# Revit family: Haworth_JiveTable_PebbleAsymmetricalLegs
name_source: partatom
category: Furniture Systems
revit_build: Autodesk Revit 2018 (Build: 20170223_1515(x64)
units: mm (PartAtom-declared; Revit-internal decimal feet)

## family parameters
Always vertical = Yes
Cut with Voids When Loaded = No
OmniClass Number = 23.40.70.14.64.21
OmniClass Title = Systems Furniture
Part Type = Normal
Room Calculation Point = No
Round Connector Dimension = Use Diameter
Shared = No
Work Plane-Based = No

## types (47) — shared parameters
48in x 108in = No
48in x 120in = No
54in x 108in = No
54in x 120in = No
54in x 144in = No
6 Column = No
8 Column = No
Actual Table Depth = 48"
Assembly Code = E2020200
Center Leg Location = 0"
Custom Size = No
Manufacturer = Haworth, Inc.
Max. Depth = 54"
Max. Height = 42"
Max. Width = 144"
Middle Columns = No
Min. Depth = 30"
Min. Height = 16"
Min. Width = 48"
Model = Haworth Jive
Revision Number = 1
Size = Verify Final Dim. w/ Haworth
Standard Depths = 24, 30, 36, 42, 48 in.
Standard Heights = 16, 20, 29 in.
Standard Widths = 48, 60, 72, 84, 96 in.
Support Depth 6 8 Column = 4 29/32"
Table Thickness = 1 3/16"
URL = http://www.haworth.com
URL - Product = http://www.haworth.com
Warranty = http://www.haworth.com

## per-type parameters (varying)
- 24d 48w 16h - Post Extruded Base - With Glides: 24in x 48in=Yes; 24in x 60in=No; 24in x 72in=No; 30in x 48in=No; 30in x 60in=No; 30in x 72in=No; 36in x 60in=No; 36in x 72in=No; 36in x 84in=No; 42in x 84in=No; 42in x 96in=No; 48in x 96in=No; Actual Depth=24"; Actual Height=16"; Actual Table Width=57"; Actual Width=48"; Casters=No; Depth=24"; Description=Haworth Jive Table Pebble Asymmetrical Legs - 24d 48w 16h - Post Extruded Base - With Glides; Glides=Yes; Height=16"; Leg Distance=6"; Leg Height=14 13/16"; Post Extruded Leg=Yes; Post Leg=Yes; Post Round Leg=No; Support Distance=11 1/2"; Support Distance 6 8 Column=1 29/32"; T Leg Extruded=No; Table Radius=12"; Width=48"
- 24d 60w 16h - Post Extruded Base - With Glides: 24in x 48in=No; 24in x 60in=Yes; 24in x 72in=No; 30in x 48in=No; 30in x 60in=No; 30in x 72in=No; 36in x 60in=No; 36in x 72in=No; 36in x 84in=No; 42in x 84in=No; 42in x 96in=No; 48in x 96in=No; Actual Depth=24"; Actual Height=16"; Actual Table Width=60"; Actual Width=60"; Casters=No; Depth=24"; Description=Haworth Jive Table Pebble Asymmetrical Legs - 24d 60w 16h - Post Extruded Base - With Glides; Glides=Yes; Height=16"; Leg Distance=6"; Leg Height=14 13/16"; Post Extruded Leg=Yes; Post Leg=Yes; Post Round Leg=No; Support Distance=11 1/2"; Support Distance 6 8 Column=4 29/32"; T Leg Extruded=No; Table Radius=12"; Width=60"
- 24d 72w 16h - Post Extruded Base - With Glides: 24in x 48in=No; 24in x 60in=No; 24in x 72in=Yes; 30in x 48in=No; 30in x 60in=No; 30in x 72in=No; 36in x 60in=No; 36in x 72in=No; 36in x 84in=No; 42in x 84in=No; 42in x 96in=No; 48in x 96in=No; Actual Depth=24"; Actual Height=16"; Actual Table Width=72"; Actual Width=72"; Casters=No; Depth=24"; Description=Haworth Jive Table Pebble Asymmetrical Legs - 24d 72w 16h - Post Extruded Base - With Glides; Glides=Yes; Height=16"; Leg Distance=6"; Leg Height=14 13/16"; Post Extruded Leg=Yes; Post Leg=Yes; Post Round Leg=No; Support Distance=11 1/2"; Support Distance 6 8 Column=16 29/32"; T Leg Extruded=No; Table Radius=12"; Width=72"
- 36d 60w 16h - Post Extruded Base - With Glides: 24in x 48in=No; 24in x 60in=No; 24in x 72in=No; 30in x 48in=No; 30in x 60in=No; 30in x 72in=No; 36in x 60in=Yes; 36in x 72in=No; 36in x 84in=No; 42in x 84in=No; 42in x 96in=No; 48in x 96in=No; Actual Depth=36"; Actual Height=16"; Actual Table Width=60"; Actual Width=60"; Casters=No; Depth=36"; Description=Haworth Jive Table Pebble Asymmetrical Legs - 36d 60w 16h - Post Extruded Base - With Glides; Glides=Yes; Height=16"; Leg Distance=12"; Leg Height=14 13/16"; Post Extruded Leg=Yes; Post Leg=Yes; Post Round Leg=No; Support Distance=11 1/2"; Support Distance 6 8 Column=4 29/32"; T Leg Extruded=No; Table Radius=18"; Width=60"
- 36d 72w 16h - Post Extruded Base - With Glides: 24in x 48in=No; 24in x 60in=No; 24in x 72in=No; 30in x 48in=No; 30in x 60in=No; 30in x 72in=No; 36in x 60in=No; 36in x 72in=Yes; 36in x 84in=No; 42in x 84in=No; 42in x 96in=No; 48in x 96in=No; Actual Depth=36"; Actual Height=16"; Actual Table Width=72"; Actual Width=72"; Casters=No; Depth=36"; Description=Haworth Jive Table Pebble Asymmetrical Legs - 36d 72w 16h - Post Extruded Base - With Glides; Glides=Yes; Height=16"; Leg Distance=12"; Leg Height=14 13/16"; Post Extruded Leg=Yes; Post Leg=Yes; Post Round Leg=No; Support Distance=11 1/2"; Support Distance 6 8 Column=16 29/32"; T Leg Extruded=No; Table Radius=18"; Width=72"
- 36d 84w 16h - Post Extruded Base - With Glides: 24in x 48in=No; 24in x 60in=No; 24in x 72in=No; 30in x 48in=No; 30in x 60in=No; 30in x 72in=No; 36in x 60in=No; 36in x 72in=No; 36in x 84in=Yes; 42in x 84in=No; 42in x 96in=No; 48in x 96in=No; Actual Depth=36"; Actual Height=16"; Actual Table Width=84"; Actual Width=84"; Casters=No; Depth=36"; Description=Haworth Jive Table Pebble Asymmetrical Legs - 36d 84w 16h - Post Extruded Base - With Glides; Glides=Yes; Height=16"; Leg Distance=12"; Leg Height=14 13/16"; Post Extruded Leg=Yes; Post Leg=Yes; Post Round Leg=No; Support Distance=11 1/2"; Support Distance 6 8 Column=28 29/32"; T Leg Extruded=No; Table Radius=18"; Width=84"
- 30d 48w 20h - Post Extruded Base - With Glides: 24in x 48in=No; 24in x 60in=No; 24in x 72in=No; 30in x 48in=Yes; 30in x 60in=No; 30in x 72in=No; 36in x 60in=No; 36in x 72in=No; 36in x 84in=No; 42in x 84in=No; 42in x 96in=No; 48in x 96in=No; Actual Depth=30"; Actual Height=20"; Actual Table Width=57"; Actual Width=48"; Casters=No; Depth=30"; Description=Haworth Jive Table Pebble Asymmetrical Legs - 30d 48w 20h - Post Extruded Base - With Glides; Glides=Yes; Height=20"; Leg Distance=9"; Leg Height=18 13/16"; Post Extruded Leg=Yes; Post Leg=Yes; Post Round Leg=No; Support Distance=11 1/2"; Support Distance 6 8 Column=1 29/32"; T Leg Extruded=No; Table Radius=15"; Width=48"
- 30d 60w 20h - Post Extruded Base - With Glides: 24in x 48in=No; 24in x 60in=No; 24in x 72in=No; 30in x 48in=No; 30in x 60in=Yes; 30in x 72in=No; 36in x 60in=No; 36in x 72in=No; 36in x 84in=No; 42in x 84in=No; 42in x 96in=No; 48in x 96in=No; Actual Depth=30"; Actual Height=20"; Actual Table Width=60"; Actual Width=60"; Casters=No; Depth=30"; Description=Haworth Jive Table Pebble Asymmetrical Legs - 30d 60w 20h - Post Extruded Base - With Glides; Glides=Yes; Height=20"; Leg Distance=9"; Leg Height=18 13/16"; Post Extruded Leg=Yes; Post Leg=Yes; Post Round Leg=No; Support Distance=11 1/2"; Support Distance 6 8 Column=4 29/32"; T Leg Extruded=No; Table Radius=15"; Width=60"
- 30d 72w 20h - Post Extruded Base - With Glides: 24in x 48in=No; 24in x 60in=No; 24in x 72in=No; 30in x 48in=No; 30in x 60in=No; 30in x 72in=Yes; 36in x 60in=No; 36in x 72in=No; 36in x 84in=No; 42in x 84in=No; 42in x 96in=No; 48in x 96in=No; Actual Depth=30"; Actual Height=20"; Actual Table Width=72"; Actual Width=72"; Casters=No; Depth=30"; Description=Haworth Jive Table Pebble Asymmetrical Legs - 30d 72w 20h - Post Extruded Base - With Glides; Glides=Yes; Height=20"; Leg Distance=9"; Leg Height=18 13/16"; Post Extruded Leg=Yes; Post Leg=Yes; Post Round Leg=No; Support Distance=11 1/2"; Support Distance 6 8 Column=16 29/32"; T Leg Extruded=No; Table Radius=15"; Width=72"
- 36d 60w 20h - Post Extruded Base - With Glides: 24in x 48in=No; 24in x 60in=No; 24in x 72in=No; 30in x 48in=No; 30in x 60in=No; 30in x 72in=No; 36in x 60in=Yes; 36in x 72in=No; 36in x 84in=No; 42in x 84in=No; 42in x 96in=No; 48in x 96in=No; Actual Depth=36"; Actual Height=20"; Actual Table Width=60"; Actual Width=60"; Casters=No; Depth=36"; Description=Haworth Jive Table Pebble Asymmetrical Legs - 36d 60w 20h - Post Extruded Base - With Glides; Glides=Yes; Height=20"; Leg Distance=12"; Leg Height=18 13/16"; Post Extruded Leg=Yes; Post Leg=Yes; Post Round Leg=No; Support Distance=11 1/2"; Support Distance 6 8 Column=4 29/32"; T Leg Extruded=No; Table Radius=18"; Width=60"
- 36d 72w 20h - Post Extruded Base - With Glides: 24in x 48in=No; 24in x 60in=No; 24in x 72in=No; 30in x 48in=No; 30in x 60in=No; 30in x 72in=No; 36in x 60in=No; 36in x 72in=Yes; 36in x 84in=No; 42in x 84in=No; 42in x 96in=No; 48in x 96in=No; Actual Depth=36"; Actual Height=20"; Actual Table Width=72"; Actual Width=72"; Casters=No; Depth=36"; Description=Haworth Jive Table Pebble Asymmetrical Legs - 36d 72w 20h - Post Extruded Base - With Glides; Glides=Yes; Height=20"; Leg Distance=12"; Leg Height=18 13/16"; Post Extruded Leg=Yes; Post Leg=Yes; Post Round Leg=No; Support Distance=11 1/2"; Support Distance 6 8 Column=16 29/32"; T Leg Extruded=No; Table Radius=18"; Width=72"
- 36d 84w 20h - Post Extruded Base - With Glides: 24in x 48in=No; 24in x 60in=No; 24in x 72in=No; 30in x 48in=No; 30in x 60in=No; 30in x 72in=No; 36in x 60in=No; 36in x 72in=No; 36in x 84in=Yes; 42in x 84in=No; 42in x 96in=No; 48in x 96in=No; Actual Depth=36"; Actual Height=20"; Actual Table Width=84"; Actual Width=84"; Casters=No; Depth=36"; Description=Haworth Jive Table Pebble Asymmetrical Legs - 36d 84w 20h - Post Extruded Base - With Glides; Glides=Yes; Height=20"; Leg Distance=12"; Leg Height=18 13/16"; Post Extruded Leg=Yes; Post Leg=Yes; Post Round Leg=No; Support Distance=11 1/2"; Support Distance 6 8 Column=28 29/32"; T Leg Extruded=No; Table Radius=18"; Width=84"
- 30d 48w 29h - Post Extruded Base - With Casters: 24in x 48in=No; 24in x 60in=No; 24in x 72in=No; 30in x 48in=Yes; 30in x 60in=No; 30in x 72in=No; 36in x 60in=No; 36in x 72in=No; 36in x 84in=No; 42in x 84in=No; 42in x 96in=No; 48in x 96in=No; Actual Depth=30"; Actual Height=29"; Actual Table Width=57"; Actual Width=48"; Casters=Yes; Depth=30"; Description=Haworth Jive Table Pebble Asymmetrical Legs - 30d 48w 29h - Post Extruded Base - With Casters; Glides=No; Height=29"; Leg Distance=9"; Leg Height=27 13/16"; Post Extruded Leg=Yes; Post Leg=Yes; Post Round Leg=No; Support Distance=11 1/2"; Support Distance 6 8 Column=1 29/32"; T Leg Extruded=No; Table Radius=15"; Width=48"
- 30d 60w 29h - Post Extruded Base - With Casters: 24in x 48in=No; 24in x 60in=No; 24in x 72in=No; 30in x 48in=No; 30in x 60in=Yes; 30in x 72in=No; 36in x 60in=No; 36in x 72in=No; 36in x 84in=No; 42in x 84in=No; 42in x 96in=No; 48in x 96in=No; Actual Depth=30"; Actual Height=29"; Actual Table Width=60"; Actual Width=60"; Casters=Yes; Depth=30"; Description=Haworth Jive Table Pebble Asymmetrical Legs - 30d 60w 29h - Post Extruded Base - With Casters; Glides=No; Height=29"; Leg Distance=9"; Leg Height=27 13/16"; Post Extruded Leg=Yes; Post Leg=Yes; Post Round Leg=No; Support Distance=11 1/2"; Support Distance 6 8 Column=4 29/32"; T Leg Extruded=No; Table Radius=15"; Width=60"
- 30d 72w 29h - Post Extruded Base - With Casters: 24in x 48in=No; 24in x 60in=No; 24in x 72in=No; 30in x 48in=No; 30in x 60in=No; 30in x 72in=Yes; 36in x 60in=No; 36in x 72in=No; 36in x 84in=No; 42in x 84in=No; 42in x 96in=No; 48in x 96in=No; Actual Depth=30"; Actual Height=29"; Actual Table Width=72"; Actual Width=72"; Casters=Yes; Depth=30"; Description=Haworth Jive Table Pebble Asymmetrical Legs - 30d 72w 29h - Post Extruded Base - With Casters; Glides=No; Height=29"; Leg Distance=9"; Leg Height=27 13/16"; Post Extruded Leg=Yes; Post Leg=Yes; Post Round Leg=No; Support Distance=11 1/2"; Support Distance 6 8 Column=16 29/32"; T Leg Extruded=No; Table Radius=15"; Width=72"
- 36d 60w 29h - Post Extruded Base - With Casters: 24in x 48in=No; 24in x 60in=No; 24in x 72in=No; 30in x 48in=No; 30in x 60in=No; 30in x 72in=No; 36in x 60in=Yes; 36in x 72in=No; 36in x 84in=No; 42in x 84in=No; 42in x 96in=No; 48in x 96in=No; Actual Depth=36"; Actual Height=29"; Actual Table Width=60"; Actual Width=60"; Casters=Yes; Depth=36"; Description=Haworth Jive Table Pebble Asymmetrical Legs - 36d 60w 29h - Post Extruded Base - With Casters; Glides=No; Height=29"; Leg Distance=12"; Leg Height=27 13/16"; Post Extruded Leg=Yes; Post Leg=Yes; Post Round Leg=No; Support Distance=11 1/2"; Support Distance 6 8 Column=4 29/32"; T Leg Extruded=No; Table Radius=18"; Width=60"
- 36d 72w 29h - Post Extruded Base - With Casters: 24in x 48in=No; 24in x 60in=No; 24in x 72in=No; 30in x 48in=No; 30in x 60in=No; 30in x 72in=No; 36in x 60in=No; 36in x 72in=Yes; 36in x 84in=No; 42in x 84in=No; 42in x 96in=No; 48in x 96in=No; Actual Depth=36"; Actual Height=29"; Actual Table Width=72"; Actual Width=72"; Casters=Yes; Depth=36"; Description=Haworth Jive Table Pebble Asymmetrical Legs - 36d 72w 29h - Post Extruded Base - With Casters; Glides=No; Height=29"; Leg Distance=12"; Leg Height=27 13/16"; Post Extruded Leg=Yes; Post Leg=Yes; Post Round Leg=No; Support Distance=11 1/2"; Support Distance 6 8 Column=16 29/32"; T Leg Extruded=No; Table Radius=18"; Width=72"
- 36d 84w 29h - Post Extruded Base - With Casters: 24in x 48in=No; 24in x 60in=No; 24in x 72in=No; 30in x 48in=No; 30in x 60in=No; 30in x 72in=No; 36in x 60in=No; 36in x 72in=No; 36in x 84in=Yes; 42in x 84in=No; 42in x 96in=No; 48in x 96in=No; Actual Depth=36"; Actual Height=29"; Actual Table Width=84"; Actual Width=84"; Casters=Yes; Depth=36"; Description=Haworth Jive Table Pebble Asymmetrical Legs - 36d 84w 29h - Post Extruded Base - With Casters; Glides=No; Height=29"; Leg Distance=12"; Leg Height=27 13/16"; Post Extruded Leg=Yes; Post Leg=Yes; Post Round Leg=No; Support Distance=11 1/2"; Support Distance 6 8 Column=28 29/32"; T Leg Extruded=No; Table Radius=18"; Width=84"
- 30d 48w 29h - Post Extruded Base - With Glides: 24in x 48in=No; 24in x 60in=No; 24in x 72in=No; 30in x 48in=Yes; 30in x 60in=No; 30in x 72in=No; 36in x 60in=No; 36in x 72in=No; 36in x 84in=No; 42in x 84in=No; 42in x 96in=No; 48in x 96in=No; Actual Depth=30"; Actual Height=29"; Actual Table Width=57"; Actual Width=48"; Casters=No; Depth=30"; Description=Haworth Jive Table Pebble Asymmetrical Legs - 30d 48w 29h - Post Extruded Base - With Glides; Glides=Yes; Height=29"; Leg Distance=9"; Leg Height=27 13/16"; Post Extruded Leg=Yes; Post Leg=Yes; Post Round Leg=No; Support Distance=11 1/2"; Support Distance 6 8 Column=1 29/32"; T Leg Extruded=No; Table Radius=15"; Width=48"
- 30d 60w 29h - Post Extruded Base - With Glides: 24in x 48in=No; 24in x 60in=No; 24in x 72in=No; 30in x 48in=No; 30in x 60in=Yes; 30in x 72in=No; 36in x 60in=No; 36in x 72in=No; 36in x 84in=No; 42in x 84in=No; 42in x 96in=No; 48in x 96in=No; Actual Depth=30"; Actual Height=29"; Actual Table Width=60"; Actual Width=60"; Casters=No; Depth=30"; Description=Haworth Jive Table Pebble Asymmetrical Legs - 30d 60w 29h - Post Extruded Base - With Glides; Glides=Yes; Height=29"; Leg Distance=9"; Leg Height=27 13/16"; Post Extruded Leg=Yes; Post Leg=Yes; Post Round Leg=No; Support Distance=11 1/2"; Support Distance 6 8 Column=4 29/32"; T Leg Extruded=No; Table Radius=15"; Width=60"
- 30d 72w 29h - Post Extruded Base - With Glides: 24in x 48in=No; 24in x 60in=No; 24in x 72in=No; 30in x 48in=No; 30in x 60in=No; 30in x 72in=Yes; 36in x 60in=No; 36in x 72in=No; 36in x 84in=No; 42in x 84in=No; 42in x 96in=No; 48in x 96in=No; Actual Depth=30"; Actual Height=29"; Actual Table Width=72"; Actual Width=72"; Casters=No; Depth=30"; Description=Haworth Jive Table Pebble Asymmetrical Legs - 30d 72w 29h - Post Extruded Base - With Glides; Glides=Yes; Height=29"; Leg Distance=9"; Leg Height=27 13/16"; Post Extruded Leg=Yes; Post Leg=Yes; Post Round Leg=No; Support Distance=11 1/2"; Support Distance 6 8 Column=16 29/32"; T Leg Extruded=No; Table Radius=15"; Width=72"
- 36d 60w 29h - Post Extruded Base - With Glides: 24in x 48in=No; 24in x 60in=No; 24in x 72in=No; 30in x 48in=No; 30in x 60in=No; 30in x 72in=No; 36in x 60in=Yes; 36in x 72in=No; 36in x 84in=No; 42in x 84in=No; 42in x 96in=No; 48in x 96in=No; Actual Depth=36"; Actual Height=29"; Actual Table Width=60"; Actual Width=60"; Casters=No; Depth=36"; Description=Haworth Jive Table Pebble Asymmetrical Legs - 36d 60w 29h - Post Extruded Base - With Glides; Glides=Yes; Height=29"; Leg Distance=12"; Leg Height=27 13/16"; Post Extruded Leg=Yes; Post Leg=Yes; Post Round Leg=No; Support Distance=11 1/2"; Support Distance 6 8 Column=4 29/32"; T Leg Extruded=No; Table Radius=18"; Width=60"
- 36d 72w 29h - Post Extruded Base - With Glides: 24in x 48in=No; 24in x 60in=No; 24in x 72in=No; 30in x 48in=No; 30in x 60in=No; 30in x 72in=No; 36in x 60in=No; 36in x 72in=Yes; 36in x 84in=No; 42in x 84in=No; 42in x 96in=No; 48in x 96in=No; Actual Depth=36"; Actual Height=29"; Actual Table Width=72"; Actual Width=72"; Casters=No; Depth=36"; Description=Haworth Jive Table Pebble Asymmetrical Legs - 36d 72w 29h - Post Extruded Base - With Glides; Glides=Yes; Height=29"; Leg Distance=12"; Leg Height=27 13/16"; Post Extruded Leg=Yes; Post Leg=Yes; Post Round Leg=No; Support Distance=11 1/2"; Support Distance 6 8 Column=16 29/32"; T Leg Extruded=No; Table Radius=18"; Width=72"
- 36d 84w 29h - Post Extruded Base - With Glides: 24in x 48in=No; 24in x 60in=No; 24in x 72in=No; 30in x 48in=No; 30in x 60in=No; 30in x 72in=No; 36in x 60in=No; 36in x 72in=No; 36in x 84in=Yes; 42in x 84in=No; 42in x 96in=No; 48in x 96in=No; Actual Depth=36"; Actual Height=29"; Actual Table Width=84"; Actual Width=84"; Casters=No; Depth=36"; Description=Haworth Jive Table Pebble Asymmetrical Legs - 36d 84w 29h - Post Extruded Base - With Glides; Glides=Yes; Height=29"; Leg Distance=12"; Leg Height=27 13/16"; Post Extruded Leg=Yes; Post Leg=Yes; Post Round Leg=No; Support Distance=11 1/2"; Support Distance 6 8 Column=28 29/32"; T Leg Extruded=No; Table Radius=18"; Width=84"
- 42d 84w 29h - Post Extruded Base - With Glides: 24in x 48in=No; 24in x 60in=No; 24in x 72in=No; 30in x 48in=No; 30in x 60in=No; 30in x 72in=No; 36in x 60in=No; 36in x 72in=No; 36in x 84in=No; 42in x 84in=Yes; 42in x 96in=No; 48in x 96in=No; Actual Depth=42"; Actual Height=29"; Actual Table Width=84"; Actual Width=84"; Casters=No; Depth=42"; Description=Haworth Jive Table Pebble Asymmetrical Legs - 42d 84w 29h - Post Extruded Base - With Glides; Glides=Yes; Height=29"; Leg Distance=15"; Leg Height=27 13/16"; Post Extruded Leg=Yes; Post Leg=Yes; Post Round Leg=No; Support Distance=11 1/2"; Support Distance 6 8 Column=28 29/32"; T Leg Extruded=No; Table Radius=21"; Width=84"
- 42d 96w 29h - Post Extruded Base - With Glides: 24in x 48in=No; 24in x 60in=No; 24in x 72in=No; 30in x 48in=No; 30in x 60in=No; 30in x 72in=No; 36in x 60in=No; 36in x 72in=No; 36in x 84in=No; 42in x 84in=No; 42in x 96in=Yes; 48in x 96in=No; Actual Depth=42"; Actual Height=29"; Actual Table Width=96"; Actual Width=96"; Casters=No; Depth=42"; Description=Haworth Jive Table Pebble Asymmetrical Legs - 42d 96w 29h - Post Extruded Base - With Glides; Glides=Yes; Height=29"; Leg Distance=15"; Leg Height=27 13/16"; Post Extruded Leg=Yes; Post Leg=Yes; Post Round Leg=No; Support Distance=11 1/2"; Support Distance 6 8 Column=40 29/32"; T Leg Extruded=No; Table Radius=21"; Width=96"
- 48d 96w 29h - Post Extruded Base - With Glides: 24in x 48in=No; 24in x 60in=No; 24in x 72in=No; 30in x 48in=No; 30in x 60in=No; 30in x 72in=No; 36in x 60in=No; 36in x 72in=No; 36in x 84in=No; 42in x 84in=No; 42in x 96in=No; 48in x 96in=Yes; Actual Depth=42"; Actual Height=29"; Actual Table Width=96"; Actual Width=96"; Casters=No; Depth=48"; Description=Haworth Jive Table Pebble Asymmetrical Legs - 48d 96w 29h - Post Extruded Base - With Glides; Glides=Yes; Height=29"; Leg Distance=15"; Leg Height=27 13/16"; Post Extruded Leg=Yes; Post Leg=Yes; Post Round Leg=No; Support Distance=11 1/2"; Support Distance 6 8 Column=40 29/32"; T Leg Extruded=No; Table Radius=21"; Width=96"
- 30d 48w 29h - Post Round Base - With Casters: 24in x 48in=No; 24in x 60in=No; 24in x 72in=No; 30in x 48in=Yes; 30in x 60in=No; 30in x 72in=No; 36in x 60in=No; 36in x 72in=No; 36in x 84in=No; 42in x 84in=No; 42in x 96in=No; 48in x 96in=No; Actual Depth=30"; Actual Height=29"; Actual Table Width=57"; Actual Width=48"; Casters=Yes; Depth=30"; Description=Haworth Jive Table Pebble Asymmetrical Legs - 30d 48w 29h - Post Round Base - With Casters; Glides=No; Height=29"; Leg Distance=9"; Leg Height=27 13/16"; Post Extruded Leg=No; Post Leg=Yes; Post Round Leg=Yes; Support Distance=11 1/2"; Support Distance 6 8 Column=1 29/32"; T Leg Extruded=No; Table Radius=15"; Width=48"
- 30d 60w 29h - Post Round Base - With Casters: 24in x 48in=No; 24in x 60in=No; 24in x 72in=No; 30in x 48in=No; 30in x 60in=Yes; 30in x 72in=No; 36in x 60in=No; 36in x 72in=No; 36in x 84in=No; 42in x 84in=No; 42in x 96in=No; 48in x 96in=No; Actual Depth=30"; Actual Height=29"; Actual Table Width=60"; Actual Width=60"; Casters=Yes; Depth=30"; Description=Haworth Jive Table Pebble Asymmetrical Legs - 30d 60w 29h - Post Round Base - With Casters; Glides=No; Height=29"; Leg Distance=9"; Leg Height=27 13/16"; Post Extruded Leg=No; Post Leg=Yes; Post Round Leg=Yes; Support Distance=11 1/2"; Support Distance 6 8 Column=4 29/32"; T Leg Extruded=No; Table Radius=15"; Width=60"
- 30d 72w 29h - Post Round Base - With Casters: 24in x 48in=No; 24in x 60in=No; 24in x 72in=No; 30in x 48in=No; 30in x 60in=No; 30in x 72in=Yes; 36in x 60in=No; 36in x 72in=No; 36in x 84in=No; 42in x 84in=No; 42in x 96in=No; 48in x 96in=No; Actual Depth=30"; Actual Height=29"; Actual Table Width=72"; Actual Width=72"; Casters=Yes; Depth=30"; Description=Haworth Jive Table Pebble Asymmetrical Legs - 30d 72w 29h - Post Round Base - With Casters; Glides=No; Height=29"; Leg Distance=9"; Leg Height=27 13/16"; Post Extruded Leg=No; Post Leg=Yes; Post Round Leg=Yes; Support Distance=11 1/2"; Support Distance 6 8 Column=16 29/32"; T Leg Extruded=No; Table Radius=15"; Width=72"
- 36d 60w 29h - Post Round Base - With Casters: 24in x 48in=No; 24in x 60in=No; 24in x 72in=No; 30in x 48in=No; 30in x 60in=No; 30in x 72in=No; 36in x 60in=Yes; 36in x 72in=No; 36in x 84in=No; 42in x 84in=No; 42in x 96in=No; 48in x 96in=No; Actual Depth=36"; Actual Height=29"; Actual Table Width=60"; Actual Width=60"; Casters=Yes; Depth=36"; Description=Haworth Jive Table Pebble Asymmetrical Legs - 36d 60w 29h - Post Round Base - With Casters; Glides=No; Height=29"; Leg Distance=12"; Leg Height=27 13/16"; Post Extruded Leg=No; Post Leg=Yes; Post Round Leg=Yes; Support Distance=11 1/2"; Support Distance 6 8 Column=4 29/32"; T Leg Extruded=No; Table Radius=18"; Width=60"
- 36d 72w 29h - Post Round Base - With Casters: 24in x 48in=No; 24in x 60in=No; 24in x 72in=No; 30in x 48in=No; 30in x 60in=No; 30in x 72in=No; 36in x 60in=No; 36in x 72in=Yes; 36in x 84in=No; 42in x 84in=No; 42in x 96in=No; 48in x 96in=No; Actual Depth=36"; Actual Height=29"; Actual Table Width=72"; Actual Width=72"; Casters=Yes; Depth=36"; Description=Haworth Jive Table Pebble Asymmetrical Legs - 36d 72w 29h - Post Round Base - With Casters; Glides=No; Height=29"; Leg Distance=12"; Leg Height=27 13/16"; Post Extruded Leg=No; Post Leg=Yes; Post Round Leg=Yes; Support Distance=11 1/2"; Support Distance 6 8 Column=16 29/32"; T Leg Extruded=No; Table Radius=18"; Width=72"
- 30d 48w 29h - Post Round Base - With Glides: 24in x 48in=No; 24in x 60in=No; 24in x 72in=No; 30in x 48in=Yes; 30in x 60in=No; 30in x 72in=No; 36in x 60in=No; 36in x 72in=No; 36in x 84in=No; 42in x 84in=No; 42in x 96in=No; 48in x 96in=No; Actual Depth=30"; Actual Height=29"; Actual Table Width=57"; Actual Width=48"; Casters=No; Depth=30"; Description=Haworth Jive Table Pebble Asymmetrical Legs - 30d 48w 29h - Post Round Base - With Glides; Glides=Yes; Height=29"; Leg Distance=9"; Leg Height=27 13/16"; Post Extruded Leg=No; Post Leg=Yes; Post Round Leg=Yes; Support Distance=11 1/2"; Support Distance 6 8 Column=1 29/32"; T Leg Extruded=No; Table Radius=15"; Width=48"
- 30d 60w 29h - Post Round Base - With Glides: 24in x 48in=No; 24in x 60in=No; 24in x 72in=No; 30in x 48in=No; 30in x 60in=Yes; 30in x 72in=No; 36in x 60in=No; 36in x 72in=No; 36in x 84in=No; 42in x 84in=No; 42in x 96in=No; 48in x 96in=No; Actual Depth=30"; Actual Height=29"; Actual Table Width=60"; Actual Width=60"; Casters=No; Depth=30"; Description=Haworth Jive Table Pebble Asymmetrical Legs - 30d 60w 29h - Post Round Base - With Glides; Glides=Yes; Height=29"; Leg Distance=9"; Leg Height=27 13/16"; Post Extruded Leg=No; Post Leg=Yes; Post Round Leg=Yes; Support Distance=11 1/2"; Support Distance 6 8 Column=4 29/32"; T Leg Extruded=No; Table Radius=15"; Width=60"
- 30d 72w 29h - Post Round Base - With Glides: 24in x 48in=No; 24in x 60in=No; 24in x 72in=No; 30in x 48in=No; 30in x 60in=No; 30in x 72in=Yes; 36in x 60in=No; 36in x 72in=No; 36in x 84in=No; 42in x 84in=No; 42in x 96in=No; 48in x 96in=No; Actual Depth=30"; Actual Height=29"; Actual Table Width=72"; Actual Width=72"; Casters=No; Depth=30"; Description=Haworth Jive Table Pebble Asymmetrical Legs - 30d 72w 29h - Post Round Base - With Glides; Glides=Yes; Height=29"; Leg Distance=9"; Leg Height=27 13/16"; Post Extruded Leg=No; Post Leg=Yes; Post Round Leg=Yes; Support Distance=11 1/2"; Support Distance 6 8 Column=16 29/32"; T Leg Extruded=No; Table Radius=15"; Width=72"
- 36d 60w 29h - Post Round Base - With Glides: 24in x 48in=No; 24in x 60in=No; 24in x 72in=No; 30in x 48in=No; 30in x 60in=No; 30in x 72in=No; 36in x 60in=Yes; 36in x 72in=No; 36in x 84in=No; 42in x 84in=No; 42in x 96in=No; 48in x 96in=No; Actual Depth=36"; Actual Height=29"; Actual Table Width=60"; Actual Width=60"; Casters=No; Depth=36"; Description=Haworth Jive Table Pebble Asymmetrical Legs - 36d 60w 29h - Post Round Base - With Glides; Glides=Yes; Height=29"; Leg Distance=12"; Leg Height=27 13/16"; Post Extruded Leg=No; Post Leg=Yes; Post Round Leg=Yes; Support Distance=11 1/2"; Support Distance 6 8 Column=4 29/32"; T Leg Extruded=No; Table Radius=18"; Width=60"
- 36d 72w 29h - Post Round Base - With Glides: 24in x 48in=No; 24in x 60in=No; 24in x 72in=No; 30in x 48in=No; 30in x 60in=No; 30in x 72in=No; 36in x 60in=No; 36in x 72in=Yes; 36in x 84in=No; 42in x 84in=No; 42in x 96in=No; 48in x 96in=No; Actual Depth=36"; Actual Height=29"; Actual Table Width=72"; Actual Width=72"; Casters=No; Depth=36"; Description=Haworth Jive Table Pebble Asymmetrical Legs - 36d 72w 29h - Post Round Base - With Glides; Glides=Yes; Height=29"; Leg Distance=12"; Leg Height=27 13/16"; Post Extruded Leg=No; Post Leg=Yes; Post Round Leg=Yes; Support Distance=11 1/2"; Support Distance 6 8 Column=16 29/32"; T Leg Extruded=No; Table Radius=18"; Width=72"
- 30d 48w 29h - T Leg Extruded - With Casters: 24in x 48in=No; 24in x 60in=No; 24in x 72in=No; 30in x 48in=Yes; 30in x 60in=No; 30in x 72in=No; 36in x 60in=No; 36in x 72in=No; 36in x 84in=No; 42in x 84in=No; 42in x 96in=No; 48in x 96in=No; Actual Depth=30"; Actual Height=29"; Actual Table Width=57"; Actual Width=48"; Casters=Yes; Depth=30"; Description=Haworth Jive Table Pebble Asymmetrical Legs - 30d 48w 29h - T Leg Extruded - With Casters; Glides=No; Height=29"; Leg Distance=9"; Leg Height=27 13/16"; Post Extruded Leg=No; Post Leg=No; Post Round Leg=No; Support Distance=11 205/256"; Support Distance 6 8 Column=1 29/32"; T Leg Extruded=Yes; Table Radius=15"; Width=48"
- 30d 60w 29h - T Leg Extruded - With Casters: 24in x 48in=No; 24in x 60in=No; 24in x 72in=No; 30in x 48in=No; 30in x 60in=Yes; 30in x 72in=No; 36in x 60in=No; 36in x 72in=No; 36in x 84in=No; 42in x 84in=No; 42in x 96in=No; 48in x 96in=No; Actual Depth=30"; Actual Height=29"; Actual Table Width=60"; Actual Width=60"; Casters=Yes; Depth=30"; Description=Haworth Jive Table Pebble Asymmetrical Legs - 30d 60w 29h - T Leg Extruded - With Casters; Glides=No; Height=29"; Leg Distance=9"; Leg Height=27 13/16"; Post Extruded Leg=No; Post Leg=No; Post Round Leg=No; Support Distance=11 205/256"; Support Distance 6 8 Column=4 29/32"; T Leg Extruded=Yes; Table Radius=15"; Width=60"
- 30d 72w 29h - T Leg Extruded - With Casters: 24in x 48in=No; 24in x 60in=No; 24in x 72in=No; 30in x 48in=No; 30in x 60in=No; 30in x 72in=Yes; 36in x 60in=No; 36in x 72in=No; 36in x 84in=No; 42in x 84in=No; 42in x 96in=No; 48in x 96in=No; Actual Depth=30"; Actual Height=29"; Actual Table Width=72"; Actual Width=72"; Casters=Yes; Depth=30"; Description=Haworth Jive Table Pebble Asymmetrical Legs - 30d 72w 29h - T Leg Extruded - With Casters; Glides=No; Height=29"; Leg Distance=9"; Leg Height=27 13/16"; Post Extruded Leg=No; Post Leg=No; Post Round Leg=No; Support Distance=11 205/256"; Support Distance 6 8 Column=16 29/32"; T Leg Extruded=Yes; Table Radius=15"; Width=72"
- 36d 60w 29h - T Leg Extruded - With Casters: 24in x 48in=No; 24in x 60in=No; 24in x 72in=No; 30in x 48in=No; 30in x 60in=No; 30in x 72in=No; 36in x 60in=Yes; 36in x 72in=No; 36in x 84in=No; 42in x 84in=No; 42in x 96in=No; 48in x 96in=No; Actual Depth=36"; Actual Height=29"; Actual Table Width=60"; Actual Width=60"; Casters=Yes; Depth=36"; Description=Haworth Jive Table Pebble Asymmetrical Legs - 36d 60w 29h - T Leg Extruded - With Casters; Glides=No; Height=29"; Leg Distance=12"; Leg Height=27 13/16"; Post Extruded Leg=No; Post Leg=No; Post Round Leg=No; Support Distance=13 205/256"; Support Distance 6 8 Column=4 29/32"; T Leg Extruded=Yes; Table Radius=18"; Width=60"
- 36d 72w 29h - T Leg Extruded - With Casters: 24in x 48in=No; 24in x 60in=No; 24in x 72in=No; 30in x 48in=No; 30in x 60in=No; 30in x 72in=No; 36in x 60in=No; 36in x 72in=Yes; 36in x 84in=No; 42in x 84in=No; 42in x 96in=No; 48in x 96in=No; Actual Depth=36"; Actual Height=29"; Actual Table Width=72"; Actual Width=72"; Casters=Yes; Depth=36"; Description=Haworth Jive Table Pebble Asymmetrical Legs - 36d 72w 29h - T Leg Extruded - With Casters; Glides=No; Height=29"; Leg Distance=12"; Leg Height=27 13/16"; Post Extruded Leg=No; Post Leg=No; Post Round Leg=No; Support Distance=13 205/256"; Support Distance 6 8 Column=16 29/32"; T Leg Extruded=Yes; Table Radius=18"; Width=72"
- 30d 48w 29h - T Leg Extruded - With Glides: 24in x 48in=No; 24in x 60in=No; 24in x 72in=No; 30in x 48in=Yes; 30in x 60in=No; 30in x 72in=No; 36in x 60in=No; 36in x 72in=No; 36in x 84in=No; 42in x 84in=No; 42in x 96in=No; 48in x 96in=No; Actual Depth=30"; Actual Height=29"; Actual Table Width=57"; Actual Width=48"; Casters=No; Depth=30"; Description=Haworth Jive Table Pebble Asymmetrical Legs - 30d 48w 29h - T Leg Extruded - With Glides; Glides=Yes; Height=29"; Leg Distance=9"; Leg Height=27 13/16"; Post Extruded Leg=No; Post Leg=No; Post Round Leg=No; Support Distance=11 205/256"; Support Distance 6 8 Column=1 29/32"; T Leg Extruded=Yes; Table Radius=15"; Width=48"
- 30d 60w 29h - T Leg Extruded - With Glides: 24in x 48in=No; 24in x 60in=No; 24in x 72in=No; 30in x 48in=No; 30in x 60in=Yes; 30in x 72in=No; 36in x 60in=No; 36in x 72in=No; 36in x 84in=No; 42in x 84in=No; 42in x 96in=No; 48in x 96in=No; Actual Depth=30"; Actual Height=29"; Actual Table Width=60"; Actual Width=60"; Casters=No; Depth=30"; Description=Haworth Jive Table Pebble Asymmetrical Legs - 30d 60w 29h - T Leg Extruded - With Glides; Glides=Yes; Height=29"; Leg Distance=9"; Leg Height=27 13/16"; Post Extruded Leg=No; Post Leg=No; Post Round Leg=No; Support Distance=11 205/256"; Support Distance 6 8 Column=4 29/32"; T Leg Extruded=Yes; Table Radius=15"; Width=60"
- 30d 72w 29h - T Leg Extruded - With Glides: 24in x 48in=No; 24in x 60in=No; 24in x 72in=No; 30in x 48in=No; 30in x 60in=No; 30in x 72in=Yes; 36in x 60in=No; 36in x 72in=No; 36in x 84in=No; 42in x 84in=No; 42in x 96in=No; 48in x 96in=No; Actual Depth=30"; Actual Height=29"; Actual Table Width=72"; Actual Width=72"; Casters=No; Depth=30"; Description=Haworth Jive Table Pebble Asymmetrical Legs - 30d 72w 29h - T Leg Extruded - With Glides; Glides=Yes; Height=29"; Leg Distance=9"; Leg Height=27 13/16"; Post Extruded Leg=No; Post Leg=No; Post Round Leg=No; Support Distance=11 205/256"; Support Distance 6 8 Column=16 29/32"; T Leg Extruded=Yes; Table Radius=15"; Width=72"
- 36d 60w 29h - T Leg Extruded - With Glides: 24in x 48in=No; 24in x 60in=No; 24in x 72in=No; 30in x 48in=No; 30in x 60in=No; 30in x 72in=No; 36in x 60in=Yes; 36in x 72in=No; 36in x 84in=No; 42in x 84in=No; 42in x 96in=No; 48in x 96in=No; Actual Depth=36"; Actual Height=29"; Actual Table Width=60"; Actual Width=60"; Casters=No; Depth=36"; Description=Haworth Jive Table Pebble Asymmetrical Legs - 36d 60w 29h - T Leg Extruded - With Glides; Glides=Yes; Height=29"; Leg Distance=12"; Leg Height=27 13/16"; Post Extruded Leg=No; Post Leg=No; Post Round Leg=No; Support Distance=13 205/256"; Support Distance 6 8 Column=4 29/32"; T Leg Extruded=Yes; Table Radius=18"; Width=60"
- 36d 72w 29h - T Leg Extruded - With Glides: 24in x 48in=No; 24in x 60in=No; 24in x 72in=No; 30in x 48in=No; 30in x 60in=No; 30in x 72in=No; 36in x 60in=No; 36in x 72in=Yes; 36in x 84in=No; 42in x 84in=No; 42in x 96in=No; 48in x 96in=No; Actual Depth=36"; Actual Height=29"; Actual Table Width=72"; Actual Width=72"; Casters=No; Depth=36"; Description=Haworth Jive Table Pebble Asymmetrical Legs - 36d 72w 29h - T Leg Extruded - With Glides; Glides=Yes; Height=29"; Leg Distance=12"; Leg Height=27 13/16"; Post Extruded Leg=No; Post Leg=No; Post Round Leg=No; Support Distance=13 205/256"; Support Distance 6 8 Column=16 29/32"; T Leg Extruded=Yes; Table Radius=18"; Width=72"

## geometry (parser evidence)
native form markers: Sweep x29
no freeform markers — native parametric forms only
